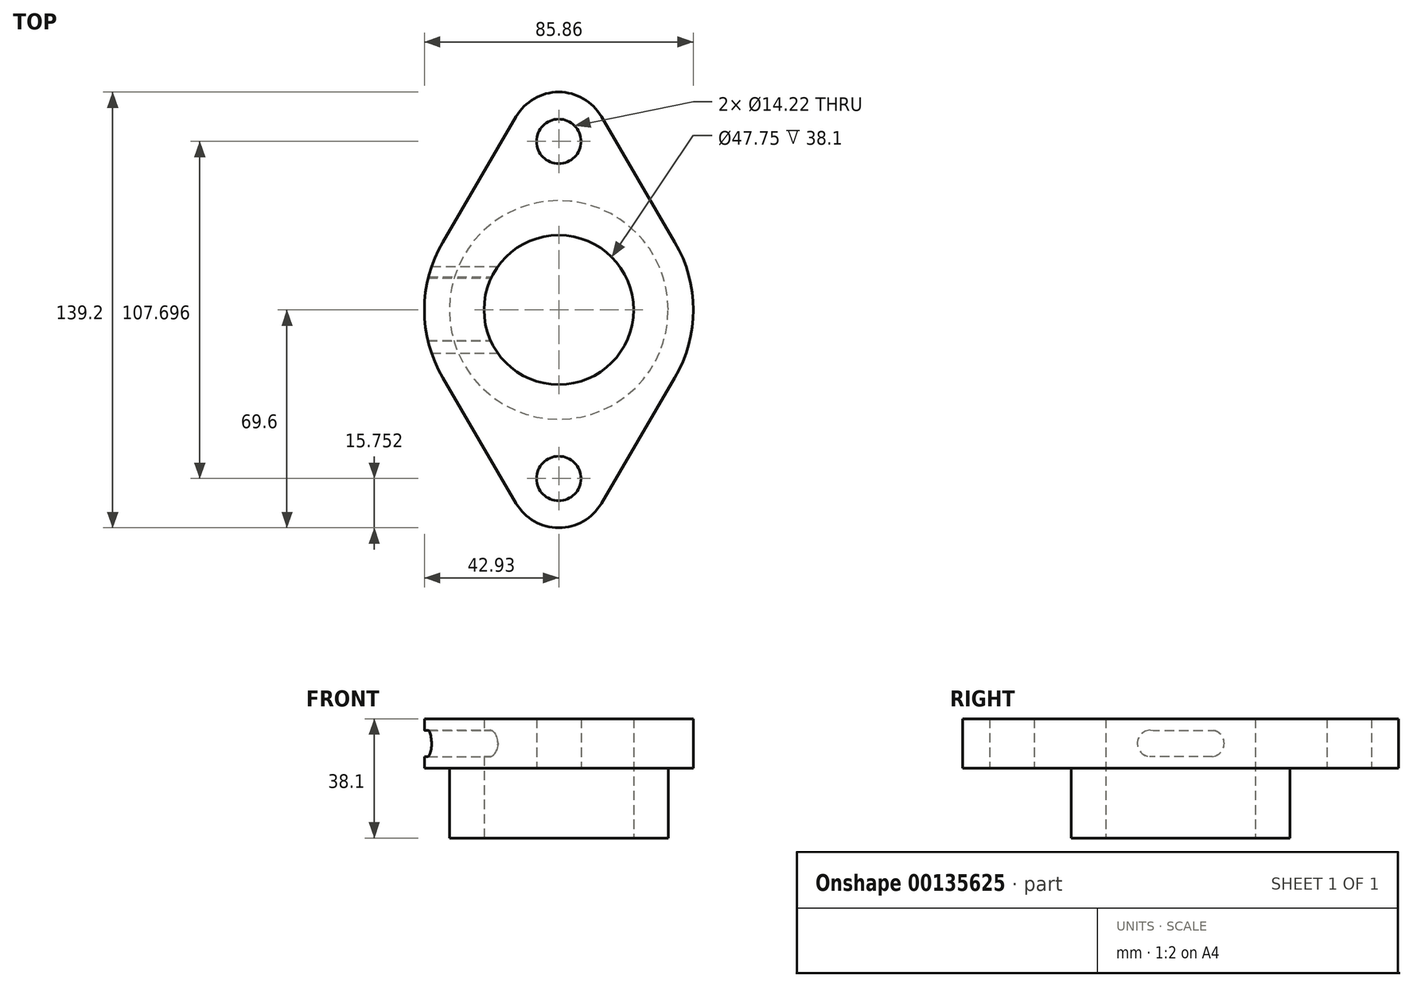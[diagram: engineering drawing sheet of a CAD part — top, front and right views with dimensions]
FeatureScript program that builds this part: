
annotation { "Feature Type Name" : "Feature", "Feature Type Description" : "" }
export const myFeature = defineFeature(function(context is Context, id is Id, definition is map)
    precondition{}
    {
        {
            var Q0;
            Q0=qCreatedBy(makeId("Top.planeOp"),FACE);
            var sketch = newSketch(context, id + "F0", { "sketchPlane" : qUnion([Q0])});
            skCircle(sketch, "E0", {"center": v(0, 0) * mm, "radius": 23.88 * mm});
            skArc(sketch, "E1", {"start": v(-37.06, 21.67) * mm, "mid": v(-42.93, 0) * mm, "end": v(-37.06, -21.67) * mm});
            skArc(sketch, "E2", {"start": v(37.06, -21.67) * mm, "mid": v(42.93, 0) * mm, "end": v(37.06, 21.67) * mm});
            skArc(sketch, "E3", {"start": v(13.6, 61.8) * mm, "mid": v(0, 69.6) * mm, "end": v(-13.6, 61.8) * mm});
            skArc(sketch, "E4", {"start": v(-13.6, -61.8) * mm, "mid": v(0, -69.6) * mm, "end": v(13.6, -61.8) * mm});
            skLineSegment(sketch, "E5", {"start": v(-37.06, 21.67) * mm, "end": v(-13.6, 61.8) * mm});
            skLineSegment(sketch, "E6", {"start": v(13.6, 61.8) * mm, "end": v(37.06, 21.67) * mm});
            skLineSegment(sketch, "E7", {"start": v(13.6, -61.8) * mm, "end": v(37.06, -21.67) * mm});
            skLineSegment(sketch, "E8", {"start": v(-13.6, -61.8) * mm, "end": v(-37.06, -21.67) * mm});
            skCircle(sketch, "E9", {"center": v(0, 53.85) * mm, "radius": 7.11 * mm});
            skCircle(sketch, "E10", {"center": v(0, -53.85) * mm, "radius": 7.11 * mm});
            skCircle(sketch, "E11", {"center": v(0, 0) * mm, "radius": 34.93 * mm});
            skSolve(sketch);
        }
        {
            var Q0;
            Q0 = qSketchRegion(id + "F0", true);
            extrude(context, id + "F1", {"entities" : qUnion([Q0]), "depth" : 15.75 * mm});
        }
        {
            var Q0;
            Q0=qCreatedBy(makeId("Top.planeOp"),FACE);
            var sketch = newSketch(context, id + "F2", { "sketchPlane" : qUnion([Q0])});
            skCircle(sketch, "E12.0", {"center": v(0, 0) * mm, "radius": 34.93 * mm});
            skCircle(sketch, "E13", {"center": v(0, 0) * mm, "radius": 23.88 * mm});
            skSolve(sketch);
        }
        {
            var Q0;
            Q0 = qSketchRegion(id + "F2", true);
            var Q1;
            Q1=makeQuery(id+"F1.opExtrude","CAP_FACE",FACE,{"disambiguationData":[OSD([sQuery(id+"F0.wireOp",EDGE,"E1"),sQuery(id+"F0.wireOp",EDGE,"E2"),sQuery(id+"F0.wireOp",EDGE,"E3"),sQuery(id+"F0.wireOp",EDGE,"E4"),sQuery(id+"F0.wireOp",EDGE,"E5"),sQuery(id+"F0.wireOp",EDGE,"E6"),sQuery(id+"F0.wireOp",EDGE,"E7"),sQuery(id+"F0.wireOp",EDGE,"E8"),sQuery(id+"F0.wireOp",EDGE,"E9"),sQuery(id+"F0.wireOp",EDGE,"E10"),sQuery(id+"F0.wireOp",EDGE,"E11")])],"isStart":false});
            extrude(context, id + "F3", {"entities" : qUnion([Q0]), "operationType" : NewBodyOperationType.ADD, "endBound" : BoundingType.UP_TO_SURFACE, "endBoundEntityFace" : qUnion([Q1]), "depth" : 25.4 * mm, "hasSecondDirection" : true, "secondDirectionOppositeDirection" : true, "secondDirectionDepth" : 22.35 * mm});
        }
        {
            var Q0;
            Q0=qCreatedBy(makeId("Right.planeOp"),FACE);
            var sketch = newSketch(context, id + "F4", { "sketchPlane" : qUnion([Q0])});
            skArc(sketch, "E14", {"start": v(-9.74, 12.08) * mm, "mid": v(-13.86, 7.96) * mm, "end": v(-9.92, 3.67) * mm});
            skArc(sketch, "E15", {"start": v(10.16, 3.7) * mm, "mid": v(13.86, 7.64) * mm, "end": v(10.62, 11.97) * mm});
            skLineSegment(sketch, "E16", {"start": v(-9.74, 12.08) * mm, "end": v(10.62, 11.97) * mm});
            skLineSegment(sketch, "E17", {"start": v(10.16, 3.7) * mm, "end": v(-9.92, 3.67) * mm});
            skSolve(sketch);
        }
        {
            var Q0;
            Q0 = qSketchRegion(id + "F4", true);
            extrude(context, id + "F5", {"entities" : qUnion([Q0]), "operationType" : NewBodyOperationType.REMOVE, "oppositeDirection" : true, "depth" : 79.38 * mm});
        }
    });
